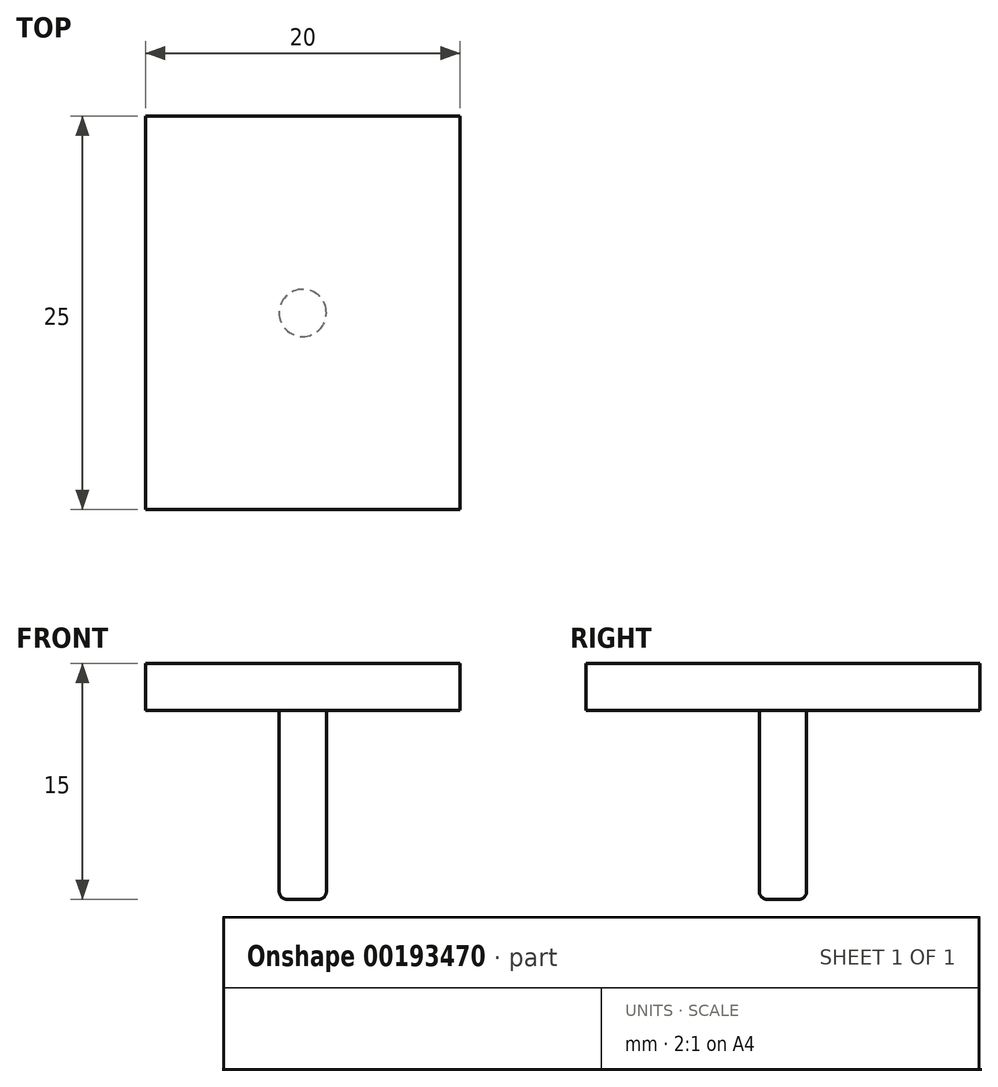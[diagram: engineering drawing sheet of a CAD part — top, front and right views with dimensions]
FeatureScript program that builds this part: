
annotation { "Feature Type Name" : "Feature", "Feature Type Description" : "" }
export const myFeature = defineFeature(function(context is Context, id is Id, definition is map)
    precondition{}
    {
        {
            var Q0;
            Q0=qCreatedBy(makeId("Top.planeOp"),FACE);
            var sketch = newSketch(context, id + "F1", { "sketchPlane" : qUnion([Q0])});
            skCircle(sketch, "E0", {"center": v(0, 0) * mm, "radius": 4.5 * mm, "construction": true});
            skLineSegment(sketch, "E1.bottom", {"start": v(10, 12.5) * mm, "end": v(-10, 12.5) * mm});
            skLineSegment(sketch, "E1.top", {"start": v(10, -12.5) * mm, "end": v(-10, -12.5) * mm});
            skLineSegment(sketch, "E1.left", {"start": v(10, 12.5) * mm, "end": v(10, -12.5) * mm});
            skLineSegment(sketch, "E1.right", {"start": v(-10, 12.5) * mm, "end": v(-10, -12.5) * mm});
            skSolve(sketch);
        }
        {
            var Q0;
            Q0=qSketchRegion(id+"F1",true);
            extrude(context, id + "F2", {"entities" : qUnion([Q0]), "depth" : 3 * mm});
        }
        {
            var Q0;
            Q0=makeQuery(id+"F2.opExtrude","CAP_FACE",FACE,{"disambiguationData":[OSD([sQuery(id+"F1.wireOp",EDGE,"E1.bottom"),sQuery(id+"F1.wireOp",EDGE,"E1.top"),sQuery(id+"F1.wireOp",EDGE,"E1.left"),sQuery(id+"F1.wireOp",EDGE,"E1.right")])],"isStart":true});
            var sketch = newSketch(context, id + "F3", { "sketchPlane" : qUnion([Q0])});
            skCircle(sketch, "E2", {"center": v(0, 0) * mm, "radius": 1.5 * mm});
            skSolve(sketch);
        }
        {
            var Q0;
            Q0=makeQuery(id+"F3.imprint","IMPRINT",FACE,{"disambiguationData":[TD([[makeQuery(id+"F3.imprint","IMPRINT",EDGE,{"derivedFrom":sQuery(id+"F3.wireOp",EDGE,"E2")}),1.0]])]});
            var Q1;
            Q1=sQuery(id+"F3.wireOp",EDGE,"E2");
            extrude(context, id + "F4", {"entities" : qUnion([Q0]), "operationType" : NewBodyOperationType.ADD, "surfaceEntities" : qUnion([Q1]), "depth" : 12 * mm});
        }
        {
            var Q0;
            Q0=makeQuery(id+"F2.opExtrude","CAP_EDGE",EDGE,{"disambiguationData":[OSD([sQuery(id+"F1.wireOp",EDGE,"E0")])],"isStart":false});
            var Q1;
            Q1=makeQuery(id+"F4.opExtrude","CAP_EDGE",EDGE,{"disambiguationData":[OSD([sQuery(id+"F3.wireOp",EDGE,"E2")])],"isStart":false});
            fillet(context, id + "F0", {"entities" : qUnion([Q0, Q1]), "radius" : 0.5 * mm, "tangentPropagation" : true, "allowEdgeOverflow" : false});
        }
    });
